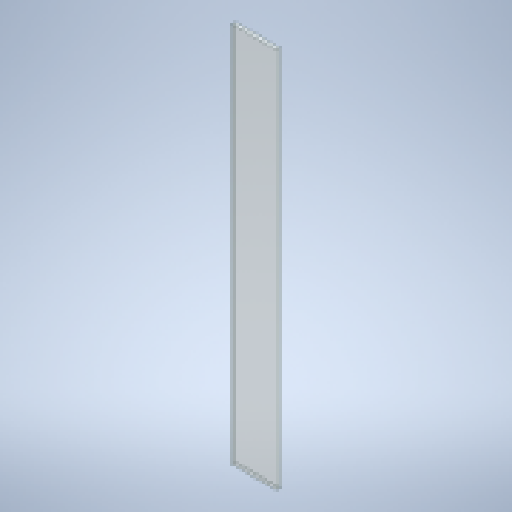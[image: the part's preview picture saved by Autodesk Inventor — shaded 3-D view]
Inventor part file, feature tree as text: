
AUTODESK INVENTOR PART (.ipt)
format: ipt  version: 2025.2 (Build 292293000, 293)  size: 257,024 bytes
history: native  units: mm
features: other x1, extrude x1, sketch x1
ambient origin geometry x8: Origin, YZ Plane, XZ Plane, XY Plane, X Axis, Y Axis, Z Axis, Center Point
bodies: Volumenkörper1 (feature_tree)
feature tree (3):
  other  "Glasscheibe"
  extrude  "Extrusion1"  TaperAngle=0.0deg  [1 undecoded]
  sketch  "Skizze1"  dims[d0=0.0mm d1=0.0mm d2=36.0mm d3=310.0mm d4=3.0mm d5=0.0mm]
note: 1 required parameter value undecoded (feature->parameter linkage not recoverable at this tier; creation-order binding heuristic only, values carry confidence <= 0.55)
